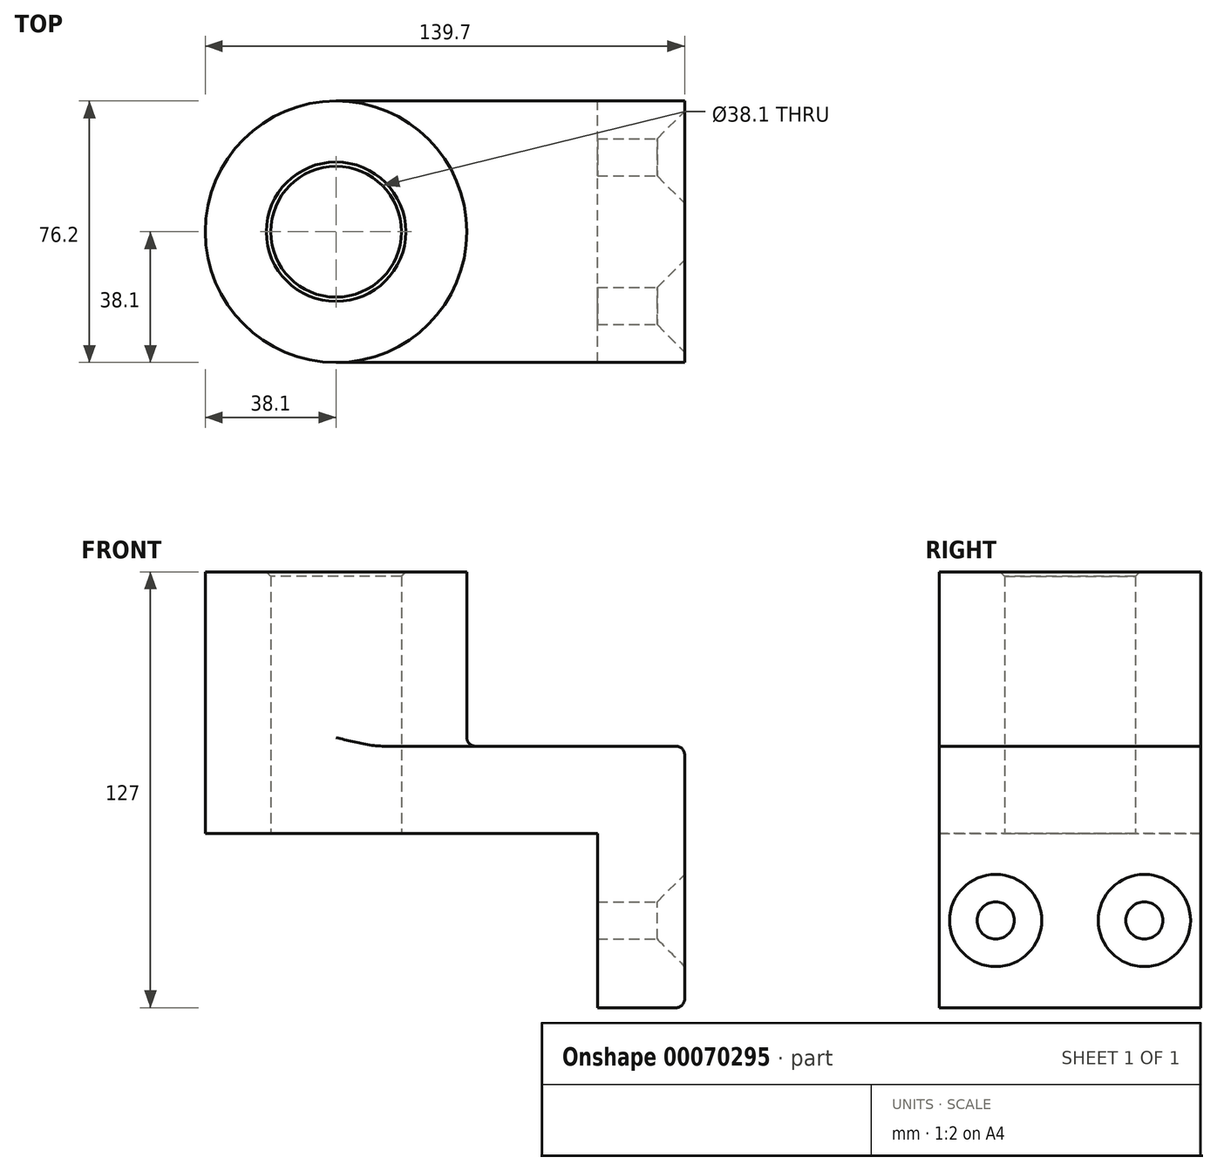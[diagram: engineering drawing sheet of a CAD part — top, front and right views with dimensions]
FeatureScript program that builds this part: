
annotation { "Feature Type Name" : "Feature", "Feature Type Description" : "" }
export const myFeature = defineFeature(function(context is Context, id is Id, definition is map)
    precondition{}
    {
        {
            var Q0;
            Q0=qCreatedBy(makeId("Top.planeOp"),FACE);
            var sketch = newSketch(context, id + "F0", { "sketchPlane" : qUnion([Q0])});
            skLineSegment(sketch, "E0.rect.bottom", {"start": v(-50.8, -38.1) * mm, "end": v(50.8, -38.1) * mm});
            skLineSegment(sketch, "E0.rect.top", {"start": v(-50.8, 38.1) * mm, "end": v(50.8, 38.1) * mm});
            skLineSegment(sketch, "E0.rect.left", {"start": v(-50.8, -38.1) * mm, "end": v(-50.8, 38.1) * mm});
            skLineSegment(sketch, "E0.rect.right", {"start": v(50.8, -38.1) * mm, "end": v(50.8, 38.1) * mm});
            skPoint(sketch, "E0.rect.middle", {"position": v(0, 0) * mm});
            skCircle(sketch, "E1", {"center": v(-50.8, 0) * mm, "radius": 38.1 * mm});
            skCircle(sketch, "E2", {"center": v(-50.8, 0) * mm, "radius": 19.05 * mm});
            skSolve(sketch);
        }
        {
            var Q0;
            Q0 = qSketchRegion(id + "F0", true);
            extrude(context, id + "F1", {"entities" : qUnion([Q0]), "depth" : 25.4 * mm});
        }
        {
            var Q0;
            {var subQ1=sQuery(id+"F0.wireOp",EDGE,"E0.rect.left");var subQ3=sQuery(id+"F0.wireOp",EDGE,"E2");var subQ4=makeQuery(id+"F0.imprint","INTERSECT",VERTEX,{"disambiguationData":[OD(0.0)],"derivedFrom":[subQ1,subQ3]});Q0=makeQuery(id+"F0.imprint","IMPRINT",FACE,{"disambiguationData":[TD([[makeQuery(id+"F0.imprint","IMPRINT",EDGE,{"disambiguationData":[TD([[subQ4,1.0]])],"derivedFrom":subQ3}),-1.0]])]});}
            var Q1;
            {var subQ1=sQuery(id+"F0.wireOp",EDGE,"E0.rect.left");var subQ3=sQuery(id+"F0.wireOp",EDGE,"E2");var subQ4=makeQuery(id+"F0.imprint","INTERSECT",VERTEX,{"disambiguationData":[OD(0.0)],"derivedFrom":[subQ1,subQ3]});Q1=makeQuery(id+"F0.imprint","IMPRINT",FACE,{"disambiguationData":[TD([[makeQuery(id+"F0.imprint","IMPRINT",EDGE,{"disambiguationData":[TD([[subQ4,-1.0]])],"derivedFrom":subQ3}),-1.0]])]});}
            extrude(context, id + "F2", {"entities" : qUnion([Q0, Q1]), "operationType" : NewBodyOperationType.ADD, "depth" : 76.2 * mm});
        }
        {
            var Q0;
            Q0=makeQuery(id+"F1.opExtrude","SWEPT_FACE",FACE,{"disambiguationData":[OSD([sQuery(id+"F0.wireOp",EDGE,"E0.rect.right")])]});
            var sketch = newSketch(context, id + "F3", { "sketchPlane" : qUnion([Q0])});
            skLineSegment(sketch, "E3.bottom", {"start": v(-38.1, 25.4) * mm, "end": v(38.1, 25.4) * mm});
            skLineSegment(sketch, "E3.top", {"start": v(-38.1, -50.8) * mm, "end": v(38.1, -50.8) * mm});
            skLineSegment(sketch, "E3.left", {"start": v(-38.1, 25.4) * mm, "end": v(-38.1, -50.8) * mm});
            skLineSegment(sketch, "E3.right", {"start": v(38.1, 25.4) * mm, "end": v(38.1, -50.8) * mm});
            skSolve(sketch);
        }
        {
            var Q0;
            Q0 = qSketchRegion(id + "F3", true);
            extrude(context, id + "F4", {"entities" : qUnion([Q0]), "operationType" : NewBodyOperationType.ADD, "oppositeDirection" : true, "depth" : 25.4 * mm});
        }
        {
            var Q0;
            Q0=makeQuery(id+"F4.boolean.opBoolean","MERGE",FACE,{"derivedFrom":[makeQuery(id+"F1.opExtrude","SWEPT_FACE",FACE,{"disambiguationData":[OSD([sQuery(id+"F0.wireOp",EDGE,"E0.rect.right")])]}),makeQuery(id+"F4.opExtrude","CAP_FACE",FACE,{"disambiguationData":[OSD([sQuery(id+"F3.wireOp",EDGE,"E3.bottom"),sQuery(id+"F3.wireOp",EDGE,"E3.top"),sQuery(id+"F3.wireOp",EDGE,"E3.left"),sQuery(id+"F3.wireOp",EDGE,"E3.right")])],"isStart":true})]});
            var sketch = newSketch(context, id + "F5", { "sketchPlane" : qUnion([Q0])});
            skPoint(sketch, "E4", {"position": v(-21.68, -25.4) * mm});
            skLineSegment(sketch, "E5", {"start": v(0, 25.4) * mm, "end": v(0, -50.8) * mm, "construction": true});
            skPoint(sketch, "E6.MirrorP", {"position": v(21.68, -25.4) * mm});
            skSolve(sketch);
        }
        {
            var Q0;
            Q0=sQuery(id+"F5.wireOp",VERTEX,"E4");
            var Q1;
            Q1=sQuery(id+"F5.wireOp",VERTEX,"E6.MirrorP");
            var Q2;
            Q2=makeQuery(id+"F1.opExtrude","SWEPT_BODY",BODY,{"disambiguationData":[OSD([sQuery(id+"F0.wireOp",EDGE,"E0.rect.bottom"),sQuery(id+"F0.wireOp",EDGE,"E0.rect.top"),sQuery(id+"F0.wireOp",EDGE,"E0.rect.right"),sQuery(id+"F0.wireOp",EDGE,"E1"),sQuery(id+"F0.wireOp",EDGE,"E2")])]});
            hole(context, id + "F6", {"style" : HoleStyle.C_SINK, "holeDiameter" : 10.8 * mm, "cSinkDiameter" : 26.88 * mm, "endStyle" : HoleEndStyle.THROUGH, "standardTappedOrClearance" : lookupTablePath({ "standard" : "ISO", "engagement" : "75%", "pitch" : "1.25 mm", "size" : "M12", "type" : "Tapped" }), "standardBlindInLast" : lookupTablePath({ "standard" : "ISO", "fit" : "Normal", "engagement" : "75%", "pitch" : "1.25 mm", "size" : "M12", "type" : "Clearance & tapped" }), "locations" : qUnion([Q0, Q1]), "scope" : qUnion([Q2]), "cSinkAngle" : 90 * degree, "majorDiameter" : 12 * mm, "showTappedDepth" : true, "isTappedThrough" : true, "tappedDepth" : 12.7 * mm, "tapClearance" : 3, "startFromSketch" : true});
        }
        {
            var Q0;
            {var subQ0=sQuery(id+"F0.wireOp",EDGE,"E1");Q0=makeQuery(id+"F2.boolean.opBoolean","INTERSECT",EDGE,{"derivedFrom":[makeQuery(id+"F1.opExtrude","CAP_FACE",FACE,{"disambiguationData":[OSD([sQuery(id+"F0.wireOp",EDGE,"E0.rect.bottom"),sQuery(id+"F0.wireOp",EDGE,"E0.rect.top"),sQuery(id+"F0.wireOp",EDGE,"E0.rect.right"),subQ0,sQuery(id+"F0.wireOp",EDGE,"E2")])],"isStart":false}),makeQuery(id+"F2.opExtrude","SWEPT_FACE",FACE,{"disambiguationData":[OSD([subQ0])]})]});}
            var Q1;
            Q1=makeQuery(id+"F1.opExtrude","CAP_EDGE",EDGE,{"disambiguationData":[OSD([sQuery(id+"F0.wireOp",EDGE,"E0.rect.right")])],"isStart":false});
            var Q2;
            Q2=makeQuery(id+"F4.opExtrude","CAP_EDGE",EDGE,{"disambiguationData":[OSD([sQuery(id+"F3.wireOp",EDGE,"E3.top")])],"isStart":true});
            fillet(context, id + "F7", {"entities" : qUnion([Q0, Q1, Q2]), "radius" : 2.54 * mm, "tangentPropagation" : true, "allowEdgeOverflow" : false});
        }
        {
            var Q0;
            Q0=makeQuery(id+"F2.opExtrude","CAP_EDGE",EDGE,{"disambiguationData":[OSD([sQuery(id+"F0.wireOp",EDGE,"E2")])],"isStart":false});
            var Q1;
            Q1=makeQuery(id+"F4.opExtrude","CAP_EDGE",EDGE,{"disambiguationData":[OSD([sQuery(id+"F3.wireOp",EDGE,"3a571342-42d4-49d0-9d47-aee1f773c3e1")])],"isStart":true});
            var Q2;
            Q2=makeQuery(id+"F4.opExtrude","CAP_EDGE",EDGE,{"disambiguationData":[OSD([sQuery(id+"F3.wireOp",EDGE,"04ea5500-ae6b-41fc-ac23-c1e66fb43d080.MirrorC")])],"isStart":true});
            chamfer(context, id + "F8", {"entities" : qUnion([Q0, Q1, Q2]), "width" : 1.27 * mm, "tangentPropagation" : true});
        }
    });
